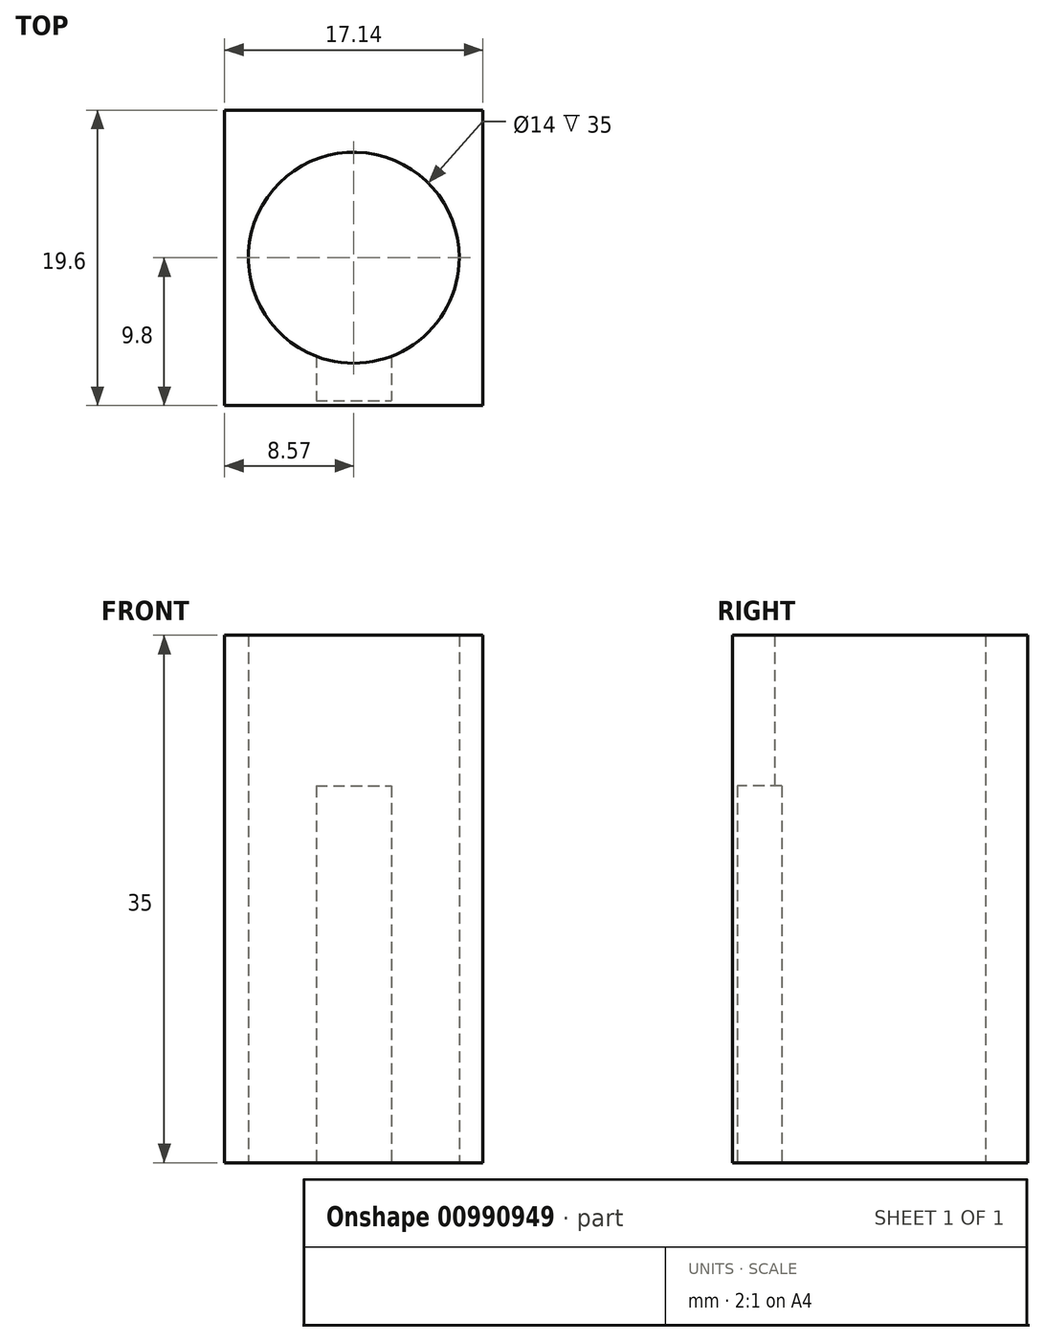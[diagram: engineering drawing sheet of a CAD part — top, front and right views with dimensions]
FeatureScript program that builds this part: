
annotation { "Feature Type Name" : "Feature", "Feature Type Description" : "" }
export const myFeature = defineFeature(function(context is Context, id is Id, definition is map)
    precondition{}
    {
        {
            var Q0;
            Q0=qCreatedBy(makeId("Top.planeOp"),FACE);
            var sketch = newSketch(context, id + "F0", { "sketchPlane" : qUnion([Q0])});
            skCircle(sketch, "E0", {"center": v(0, 0) * mm, "radius": 7 * mm});
            skLineSegment(sketch, "E1.bottom", {"start": v(8.57, -9.8) * mm, "end": v(-8.57, -9.8) * mm});
            skLineSegment(sketch, "E1.top", {"start": v(8.57, 9.8) * mm, "end": v(-8.57, 9.8) * mm});
            skLineSegment(sketch, "E1.left", {"start": v(8.57, -9.8) * mm, "end": v(8.57, 9.8) * mm});
            skLineSegment(sketch, "E1.right", {"start": v(-8.57, -9.8) * mm, "end": v(-8.57, 9.8) * mm});
            skLineSegment(sketch, "E2", {"start": v(0, 11.31) * mm, "end": v(0, -11.81) * mm, "construction": true});
            skLineSegment(sketch, "E3", {"start": v(-2.5, -6.54) * mm, "end": v(-2.5, -9.5) * mm});
            skLineSegment(sketch, "E4", {"start": v(-2.5, -9.5) * mm, "end": v(0, -9.5) * mm});
            skLineSegment(sketch, "E5.MirrorCS", {"start": v(2.5, -9.5) * mm, "end": v(0, -9.5) * mm});
            skLineSegment(sketch, "E6.MirrorCS", {"start": v(2.5, -6.54) * mm, "end": v(2.5, -9.5) * mm});
            skPoint(sketch, "E7", {"position": v(0, -7) * mm});
            skSolve(sketch);
        }
        {
            var Q0;
            Q0=makeQuery(id+"F0.imprint","IMPRINT",FACE,{"disambiguationData":[TD([[makeQuery(id+"F0.imprint","IMPRINT",EDGE,{"derivedFrom":sQuery(id+"F0.wireOp",EDGE,"E1.bottom")}),-1.0]])]});
            var Q1;
            {var subQ0=sQuery(id+"F0.wireOp",EDGE,"E0");var subQ2=makeQuery(id+"F0.imprint","IMPRINT",VERTEX,{"derivedFrom":subQ0});Q1=makeQuery(id+"F0.imprint","IMPRINT",FACE,{"disambiguationData":[TD([[makeQuery(id+"F0.imprint","IMPRINT",EDGE,{"disambiguationData":[TD([[subQ2,-1.0]])],"derivedFrom":subQ0}),1.0]])]});}
            var Q2;
            {var subQ0=sQuery(id+"F0.wireOp",EDGE,"E3");Q2=makeQuery(id+"F0.imprint","IMPRINT",FACE,{"disambiguationData":[TD([[makeQuery(id+"F0.imprint","IMPRINT",EDGE,{"derivedFrom":subQ0}),1.0]])]});}
            extrude(context, id + "F1", {"entities" : qUnion([Q0, Q1, Q2]), "depth" : 35 * mm, "offsetDistance" : 25 * mm});
        }
        {
            var Q0;
            {var subQ0=sQuery(id+"F0.wireOp",EDGE,"E0");var subQ2=makeQuery(id+"F0.imprint","IMPRINT",VERTEX,{"derivedFrom":subQ0});Q0=makeQuery(id+"F0.imprint","IMPRINT",FACE,{"disambiguationData":[TD([[makeQuery(id+"F0.imprint","IMPRINT",EDGE,{"disambiguationData":[TD([[subQ2,-1.0]])],"derivedFrom":subQ0}),1.0]])]});}
            var Q1;
            {var subQ0=sQuery(id+"F0.wireOp",EDGE,"E3");Q1=makeQuery(id+"F0.imprint","IMPRINT",FACE,{"disambiguationData":[TD([[makeQuery(id+"F0.imprint","IMPRINT",EDGE,{"derivedFrom":subQ0}),1.0]])]});}
            extrude(context, id + "F2", {"entities" : qUnion([Q0, Q1]), "operationType" : NewBodyOperationType.REMOVE, "depth" : 25 * mm, "offsetDistance" : 25 * mm});
        }
    });
